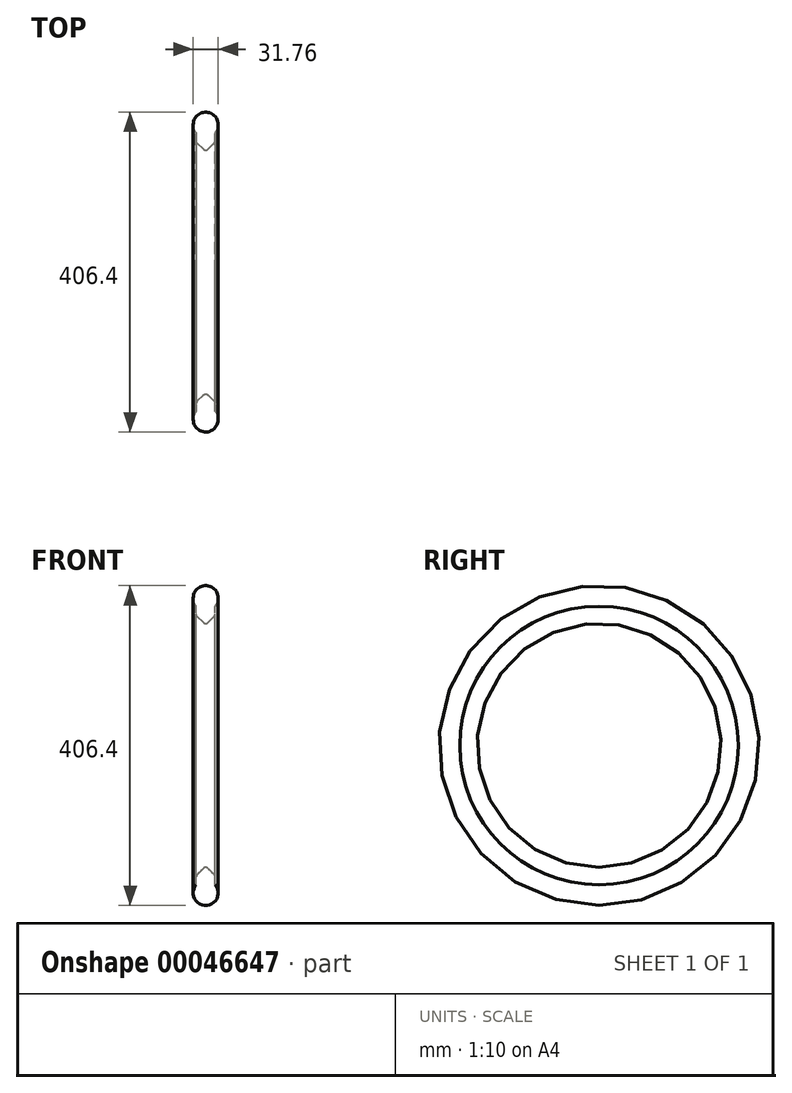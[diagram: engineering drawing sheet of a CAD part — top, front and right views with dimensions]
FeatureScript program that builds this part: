
annotation { "Feature Type Name" : "Feature", "Feature Type Description" : "" }
export const myFeature = defineFeature(function(context is Context, id is Id, definition is map)
    precondition{}
    {
        {
            var Q0;
            Q0=qCreatedBy(makeId("Top.planeOp"),FACE);
            var sketch = newSketch(context, id + "F0", { "sketchPlane" : qUnion([Q0])});
            skLineSegment(sketch, "E0", {"start": v(-2.83, -156.1) * mm, "end": v(-10.83, -164.1) * mm});
            skLineSegment(sketch, "E1", {"start": v(-12, -166.93) * mm, "end": v(-12, -176.93) * mm});
            skLineSegment(sketch, "E2", {"start": v(0, 0) * mm, "end": v(-14.2, 0) * mm, "construction": true});
            skLineSegment(sketch, "E3", {"start": v(0, -44.58) * mm, "end": v(0, -153.28) * mm, "construction": true});
            skLineSegment(sketch, "E4.MirrorCS", {"start": v(2.83, -156.1) * mm, "end": v(10.83, -164.1) * mm});
            skLineSegment(sketch, "E5.MirrorCS", {"start": v(12, -166.93) * mm, "end": v(12, -176.93) * mm});
            skLineSegment(sketch, "E6", {"start": v(-12, -176.93) * mm, "end": v(12, -176.93) * mm, "construction": true});
            skPoint(sketch, "E7.visualSharp", {"position": v(0, -153.28) * mm});
            skArc(sketch, "E7.filletArc", {"start": v(2.83, -156.1) * mm, "mid": v(0, -154.93) * mm, "end": v(-2.83, -156.1) * mm});
            skPoint(sketch, "E8", {"position": v(0, -174.5) * mm});
            skPoint(sketch, "E9.visualSharp", {"position": v(12, -165.28) * mm});
            skArc(sketch, "E9.filletArc", {"start": v(12, -166.93) * mm, "mid": v(11.7, -165.4) * mm, "end": v(10.83, -164.1) * mm});
            skPoint(sketch, "E10.visualSharp", {"position": v(-12, -165.28) * mm});
            skArc(sketch, "E10.filletArc", {"start": v(-10.83, -164.1) * mm, "mid": v(-11.7, -165.4) * mm, "end": v(-12, -166.93) * mm});
            skArc(sketch, "E11", {"start": v(-12, -176.93) * mm, "mid": v(0, -203.2) * mm, "end": v(12, -176.93) * mm});
            skSolve(sketch);
        }
        {
            var Q0;
            Q0=qSketchRegion(id+"F0",true);
            var Q1;
            Q1=sQuery(id+"F0.wireOp",EDGE,"E2");
            revolve(context, id + "F1", {"entities" : qUnion([Q0]), "axis" : qUnion([Q1]), "revolveType" : RevolveType.FULL});
        }
    });
